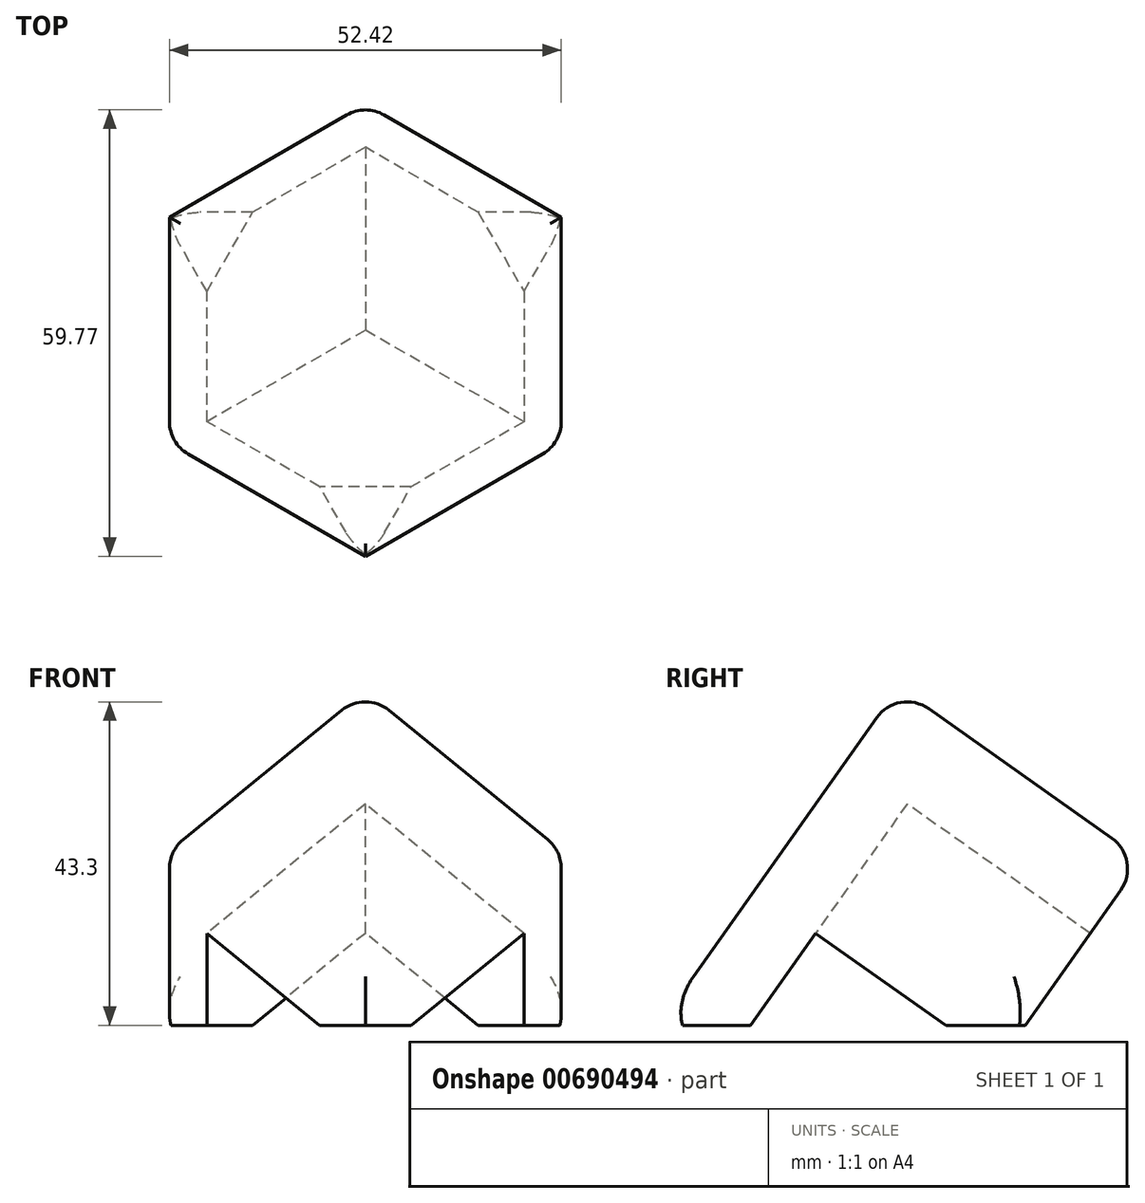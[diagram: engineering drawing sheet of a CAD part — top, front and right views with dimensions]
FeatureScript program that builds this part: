
annotation { "Feature Type Name" : "Feature", "Feature Type Description" : "" }
export const myFeature = defineFeature(function(context is Context, id is Id, definition is map)
    precondition{}
    {
        {
            var Q0;
            Q0=qCreatedBy(makeId("Top.planeOp"),FACE);
            var sketch = newSketch(context, id + "F0", { "sketchPlane" : qUnion([Q0])});
            skLineSegment(sketch, "E0.bottom", {"start": v(0, 0) * mm, "end": v(40, 0) * mm});
            skLineSegment(sketch, "E0.top", {"start": v(0, 40) * mm, "end": v(40, 40) * mm});
            skLineSegment(sketch, "E0.left", {"start": v(0, 0) * mm, "end": v(0, 40) * mm});
            skLineSegment(sketch, "E0.right", {"start": v(40, 0) * mm, "end": v(40, 40) * mm});
            skSolve(sketch);
        }
        {
            var Q0;
            Q0=makeQuery(id+"F0.imprint","IMPRINT",FACE,{"disambiguationData":[TD([[makeQuery(id+"F0.imprint","IMPRINT",EDGE,{"derivedFrom":sQuery(id+"F0.wireOp",EDGE,"E0.bottom")}),1.0]])]});
            extrude(context, id + "F1", {"entities" : qUnion([Q0]), "depth" : 10 * mm, "offsetDistance" : 25 * mm});
        }
        {
            var Q0;
            Q0=makeQuery(id+"F1.opExtrude","CAP_FACE",FACE,{"disambiguationData":[OSD([sQuery(id+"F0.wireOp",EDGE,"E0.bottom"),sQuery(id+"F0.wireOp",EDGE,"E0.top"),sQuery(id+"F0.wireOp",EDGE,"E0.left"),sQuery(id+"F0.wireOp",EDGE,"E0.right")])],"isStart":false});
            var sketch = newSketch(context, id + "F2", { "sketchPlane" : qUnion([Q0])});
            skLineSegment(sketch, "E1", {"start": v(0, 0) * mm, "end": v(0, 40) * mm});
            skLineSegment(sketch, "E2", {"start": v(0, 40) * mm, "end": v(10, 40) * mm});
            skLineSegment(sketch, "E3", {"start": v(10, 40) * mm, "end": v(10, 10) * mm});
            skLineSegment(sketch, "E4", {"start": v(10, 10) * mm, "end": v(40, 10) * mm});
            skLineSegment(sketch, "E5", {"start": v(40, 10) * mm, "end": v(40, 0) * mm});
            skLineSegment(sketch, "E6", {"start": v(40, 0) * mm, "end": v(0, 0) * mm});
            skSolve(sketch);
        }
        {
            var Q0;
            Q0=makeQuery(id+"F2.imprint","IMPRINT",FACE,{"disambiguationData":[TD([[makeQuery(id+"F2.imprint","IMPRINT",EDGE,{"derivedFrom":sQuery(id+"F2.wireOp",EDGE,"E1")}),-1.0]])]});
            extrude(context, id + "F3", {"entities" : qUnion([Q0]), "operationType" : NewBodyOperationType.ADD, "depth" : 30 * mm, "offsetDistance" : 25 * mm});
        }
        {
            var Q0;
            Q0=makeQuery(id+"F3.opExtrude","CAP_EDGE",EDGE,{"disambiguationData":[OSD([sQuery(id+"F2.wireOp",EDGE,"E6")])],"isStart":false});
            var Q1;
            Q1=makeQuery(id+"F3.opExtrude","CAP_EDGE",EDGE,{"disambiguationData":[OSD([sQuery(id+"F2.wireOp",EDGE,"E1")])],"isStart":false});
            var Q2;
            Q2=makeQuery(id+"F3.boolean.opBoolean","MERGE",EDGE,{"derivedFrom":[makeQuery(id+"F1.opExtrude","SWEPT_EDGE",EDGE,{"disambiguationData":[OSD([sQuery(id+"F0.wireOp",EDGE,"E0.bottom"),sQuery(id+"F0.wireOp",EDGE,"E0.left")])]}),makeQuery(id+"F3.opExtrude","SWEPT_EDGE",EDGE,{"disambiguationData":[OSD([sQuery(id+"F2.wireOp",EDGE,"E1"),sQuery(id+"F2.wireOp",EDGE,"E6")])]})]});
            var Q3;
            Q3=makeQuery(id+"F1.opExtrude","CAP_EDGE",EDGE,{"disambiguationData":[OSD([sQuery(id+"F0.wireOp",EDGE,"E0.bottom")])],"isStart":true});
            var Q4;
            Q4=makeQuery(id+"F1.opExtrude","CAP_EDGE",EDGE,{"disambiguationData":[OSD([sQuery(id+"F0.wireOp",EDGE,"E0.left")])],"isStart":true});
            var Q5;
            Q5=makeQuery(id+"F1.opExtrude","CAP_EDGE",EDGE,{"disambiguationData":[OSD([sQuery(id+"F0.wireOp",EDGE,"E0.top")])],"isStart":true});
            var Q6;
            Q6=makeQuery(id+"F1.opExtrude","CAP_EDGE",EDGE,{"disambiguationData":[OSD([sQuery(id+"F0.wireOp",EDGE,"E0.right")])],"isStart":true});
            var Q7;
            Q7=makeQuery(id+"F3.boolean.opBoolean","MERGE",EDGE,{"derivedFrom":[makeQuery(id+"F1.opExtrude","SWEPT_EDGE",EDGE,{"disambiguationData":[OSD([sQuery(id+"F0.wireOp",EDGE,"E0.bottom"),sQuery(id+"F0.wireOp",EDGE,"E0.right")])]}),makeQuery(id+"F3.opExtrude","SWEPT_EDGE",EDGE,{"disambiguationData":[OSD([sQuery(id+"F2.wireOp",EDGE,"E5"),sQuery(id+"F2.wireOp",EDGE,"E6")])]})]});
            var Q8;
            Q8=makeQuery(id+"F3.boolean.opBoolean","MERGE",EDGE,{"derivedFrom":[makeQuery(id+"F1.opExtrude","SWEPT_EDGE",EDGE,{"disambiguationData":[OSD([sQuery(id+"F0.wireOp",EDGE,"E0.top"),sQuery(id+"F0.wireOp",EDGE,"E0.left")])]}),makeQuery(id+"F3.opExtrude","SWEPT_EDGE",EDGE,{"disambiguationData":[OSD([sQuery(id+"F2.wireOp",EDGE,"E1"),sQuery(id+"F2.wireOp",EDGE,"E2")])]})]});
            fillet(context, id + "F4", {"entities" : qUnion([Q0, Q1, Q2, Q3, Q4, Q5, Q6, Q7, Q8]), "radius" : 5 * mm, "tangentPropagation" : true, "allowEdgeOverflow" : false});
        }
        {
            var Q0;
            Q0=makeQuery(id+"F1.opExtrude","CAP_VERTEX",VERTEX,{"disambiguationData":[OSD([sQuery(id+"F0.wireOp",EDGE,"E0.top"),sQuery(id+"F0.wireOp",EDGE,"E0.right")])],"isStart":false});
            var Q1;
            Q1=makeQuery(id+"F3.opExtrude","CAP_VERTEX",VERTEX,{"disambiguationData":[OSD([sQuery(id+"F0.wireOp",EDGE,"E0.right"),sQuery(id+"F2.wireOp",EDGE,"E4"),sQuery(id+"F2.wireOp",EDGE,"E5")])],"isStart":false});
            var Q2;
            Q2=makeQuery(id+"F3.opExtrude","CAP_VERTEX",VERTEX,{"disambiguationData":[OSD([sQuery(id+"F0.wireOp",EDGE,"E0.top"),sQuery(id+"F2.wireOp",EDGE,"E2"),sQuery(id+"F2.wireOp",EDGE,"E3")])],"isStart":false});
            cPlane(context, id + "F5", {"entities" : qUnion([Q0, Q1, Q2]), "cplaneType" : CPlaneType.THREE_POINT, "offset" : 25 * mm, "width" : 150 * mm, "height" : 150 * mm});
        }
        {
            var Q0;
            Q0=qCreatedBy(id+"F5.planeOp",FACE);
            var sketch = newSketch(context, id + "F6", { "sketchPlane" : qUnion([Q0])});
            skCircle(sketch, "E7", {"center": v(0, 0) * mm, "radius": 32.5 * mm});
            skSolve(sketch);
        }
        {
            var Q0;
            Q0=makeQuery(id+"F6.imprint","IMPRINT",FACE,{"disambiguationData":[TD([[makeQuery(id+"F6.imprint","IMPRINT",EDGE,{"derivedFrom":sQuery(id+"F6.wireOp",EDGE,"E7")}),1.0]])]});
            var Q1;
            Q1=makeQuery(id+"F1.opExtrude","CAP_VERTEX",VERTEX,{"disambiguationData":[OSD([sQuery(id+"F0.wireOp",EDGE,"E0.top"),sQuery(id+"F0.wireOp",EDGE,"E0.right")])],"isStart":true});
            extrude(context, id + "F7", {"entities" : qUnion([Q0]), "operationType" : NewBodyOperationType.REMOVE, "oppositeDirection" : true, "depth" : 5 * mm, "endBoundEntityVertex" : qUnion([Q1]), "offsetDistance" : 25 * mm});
        }
        {
            var Q0;
            Q0=qCreatedBy(makeId("Top.planeOp"),FACE);
            var sketch = newSketch(context, id + "F8", { "sketchPlane" : qUnion([Q0])});
            skLineSegment(sketch, "E8", {"start": v(0, 0) * mm, "end": v(0, 55) * mm, "construction": true});
            skLineSegment(sketch, "E9", {"start": v(0, 0) * mm, "end": v(55, 0) * mm, "construction": true});
            skSolve(sketch);
        }
        {
            var Q0;
            Q0=makeQuery(id+"F1.opExtrude","SWEPT_BODY",BODY,{"disambiguationData":[OSD([sQuery(id+"F0.wireOp",EDGE,"E0.bottom"),sQuery(id+"F0.wireOp",EDGE,"E0.top"),sQuery(id+"F0.wireOp",EDGE,"E0.left"),sQuery(id+"F0.wireOp",EDGE,"E0.right")])]});
            var Q1;
            Q1=sQuery(id+"F8.wireOp",EDGE,"E8");
            var Q2;
            Q2=sQuery(id+"F8.wireOp",EDGE,"E8");
            transform(context, id + "F9", {"entities" : qUnion([Q0]), "transformType" : TransformType.ROTATION, "transformAxis" : qUnion([Q2]), "angle" : 225 * degree, "oppositeDirection" : true, "makeCopy" : false});
        }
        {
            var Q0;
            Q0=makeQuery(id+"F1.opExtrude","SWEPT_BODY",BODY,{"disambiguationData":[OSD([sQuery(id+"F0.wireOp",EDGE,"E0.bottom"),sQuery(id+"F0.wireOp",EDGE,"E0.top"),sQuery(id+"F0.wireOp",EDGE,"E0.left"),sQuery(id+"F0.wireOp",EDGE,"E0.right")])]});
            var Q1;
            Q1=sQuery(id+"F8.wireOp",EDGE,"E9");
            transform(context, id + "F10", {"entities" : qUnion([Q0]), "transformType" : TransformType.ROTATION, "transformAxis" : qUnion([Q1]), "angle" : 35.26 * degree, "oppositeDirection" : true, "makeCopy" : false});
        }
        {
            var Q0;
            Q0=makeQuery(id+"F7.boolean.opBoolean","INTERSECT",EDGE,{"derivedFrom":[makeQuery(id+"F1.opExtrude","CAP_FACE",FACE,{"disambiguationData":[OSD([sQuery(id+"F0.wireOp",EDGE,"E0.bottom"),sQuery(id+"F0.wireOp",EDGE,"E0.top"),sQuery(id+"F0.wireOp",EDGE,"E0.left"),sQuery(id+"F0.wireOp",EDGE,"E0.right")])],"isStart":false}),makeQuery(id+"F7.opExtrude","CAP_FACE",FACE,{"disambiguationData":[OSD([sQuery(id+"F6.wireOp",EDGE,"E7")])],"isStart":false})]});
            cPoint(context, id + "F11", {"entities" : qUnion([Q0]), "parameter" : 0.5});
        }
        {
            var Q0;
            Q0=qCreatedBy(makeId("Top.planeOp"),FACE);
            var Q1;
            Q1 = qCreatedBy(id + "F11" ,VERTEX);
            cPlane(context, id + "F12", {"entities" : qUnion([Q0, Q1]), "cplaneType" : CPlaneType.PLANE_POINT, "offset" : 25 * mm, "width" : 150 * mm, "height" : 150 * mm});
        }
        {
            var Q0;
            Q0=makeQuery(id+"F1.opExtrude","SWEPT_BODY",BODY,{"disambiguationData":[OSD([sQuery(id+"F0.wireOp",EDGE,"E0.bottom"),sQuery(id+"F0.wireOp",EDGE,"E0.top"),sQuery(id+"F0.wireOp",EDGE,"E0.left"),sQuery(id+"F0.wireOp",EDGE,"E0.right")])]});
            transform(context, id + "F13", {"entities" : qUnion([Q0]), "transformType" : TransformType.TRANSLATION_3D, "dx" : 0 * mm, "dy" : 0 * mm, "dz" : 46.96 * mm, "makeCopy" : false});
        }
    });
